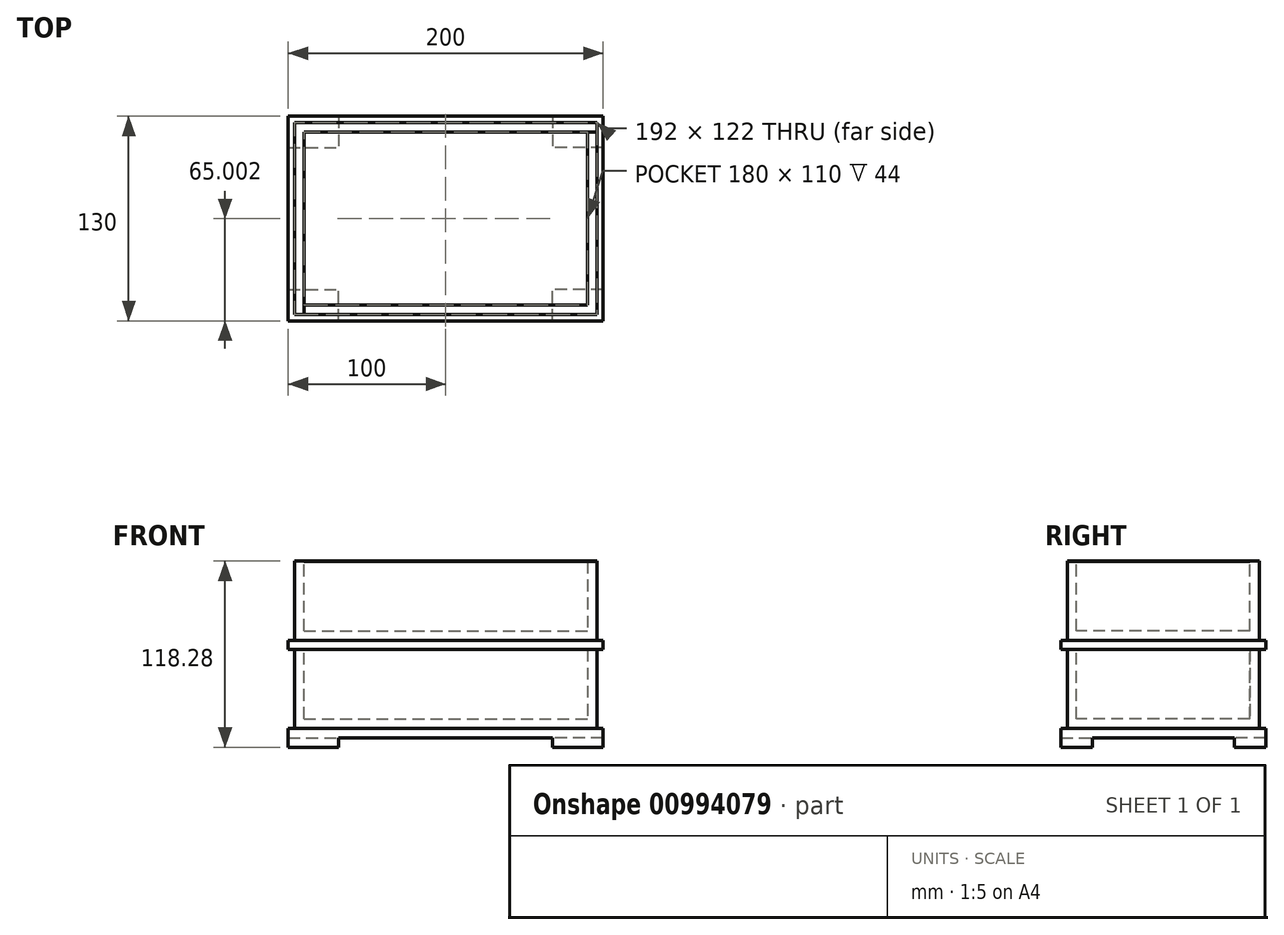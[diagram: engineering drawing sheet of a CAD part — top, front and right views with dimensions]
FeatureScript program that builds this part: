
annotation { "Feature Type Name" : "Feature", "Feature Type Description" : "" }
export const myFeature = defineFeature(function(context is Context, id is Id, definition is map)
    precondition{}
    {
        {
            var Q0;
            Q0=qCreatedBy(makeId("Top.planeOp"),FACE);
            var sketch = newSketch(context, id + "F0", { "sketchPlane" : qUnion([Q0])});
            skLineSegment(sketch, "E0.bottom", {"start": v(-113.27, 130.86) * mm, "end": v(66.73, 130.86) * mm});
            skLineSegment(sketch, "E0.top", {"start": v(-113.27, 20.86) * mm, "end": v(66.73, 20.86) * mm});
            skLineSegment(sketch, "E0.left", {"start": v(-113.27, 130.86) * mm, "end": v(-113.27, 20.86) * mm});
            skLineSegment(sketch, "E0.right", {"start": v(66.73, 130.86) * mm, "end": v(66.73, 20.86) * mm});
            skSolve(sketch);
        }
        {
            var Q0;
            Q0=makeQuery(id+"F0.imprint","IMPRINT",FACE,{"disambiguationData":[TD([[makeQuery(id+"F0.imprint","IMPRINT",EDGE,{"derivedFrom":sQuery(id+"F0.wireOp",EDGE,"E0.bottom")}),-1.0]])]});
            extrude(context, id + "F1", {"entities" : qUnion([Q0]), "depth" : 6 * mm, "offsetDistance" : 25 * mm});
        }
        {
            var Q0;
            Q0=makeQuery(id+"F1.opExtrude","SWEPT_FACE",FACE,{"disambiguationData":[OSD([sQuery(id+"F0.wireOp",EDGE,"E0.top")])]});
            var sketch = newSketch(context, id + "F2", { "sketchPlane" : qUnion([Q0])});
            skLineSegment(sketch, "E1.bottom", {"start": v(-113.27, 0) * mm, "end": v(66.73, 0) * mm});
            skLineSegment(sketch, "E1.top", {"start": v(-113.27, 50) * mm, "end": v(66.73, 50) * mm});
            skLineSegment(sketch, "E1.left", {"start": v(-113.27, 0) * mm, "end": v(-113.27, 50) * mm});
            skLineSegment(sketch, "E1.right", {"start": v(66.73, 0) * mm, "end": v(66.73, 50) * mm});
            skSolve(sketch);
        }
        {
            var Q0;
            {var subQ0=sQuery(id+"F2.wireOp",EDGE,"E1.top");Q0=makeQuery(id+"F2.imprint","IMPRINT",FACE,{"disambiguationData":[TD([[makeQuery(id+"F2.imprint","IMPRINT",EDGE,{"derivedFrom":subQ0}),-1.0]])]});}
            var Q1;
            {var subQ0=sQuery(id+"F2.wireOp",EDGE,"E1.bottom");Q1=makeQuery(id+"F2.imprint","IMPRINT",FACE,{"disambiguationData":[TD([[makeQuery(id+"F2.imprint","IMPRINT",EDGE,{"derivedFrom":subQ0}),1.0]])]});}
            extrude(context, id + "F3", {"entities" : qUnion([Q0, Q1]), "depth" : 6 * mm, "offsetDistance" : 25 * mm});
        }
        {
            var Q0;
            Q0=makeQuery(id+"F3.opExtrude","SWEPT_FACE",FACE,{"disambiguationData":[OSD([sQuery(id+"F2.wireOp",EDGE,"E1.right")])]});
            var sketch = newSketch(context, id + "F4", { "sketchPlane" : qUnion([Q0])});
            skLineSegment(sketch, "E2.bottom", {"start": v(14.86, 50) * mm, "end": v(130.86, 50) * mm});
            skLineSegment(sketch, "E2.top", {"start": v(14.86, 0) * mm, "end": v(130.86, 0) * mm});
            skLineSegment(sketch, "E2.left", {"start": v(14.86, 50) * mm, "end": v(14.86, 0) * mm});
            skLineSegment(sketch, "E2.right", {"start": v(130.86, 50) * mm, "end": v(130.86, 0) * mm});
            skSolve(sketch);
        }
        {
            var Q0;
            {var subQ2=sQuery(id+"F4.wireOp",EDGE,"E2.right");Q0=makeQuery(id+"F4.imprint","IMPRINT",FACE,{"disambiguationData":[TD([[makeQuery(id+"F4.imprint","IMPRINT",EDGE,{"derivedFrom":subQ2}),-1.0]])]});}
            var Q1;
            {var subQ2=sQuery(id+"F4.wireOp",EDGE,"E2.left");Q1=makeQuery(id+"F4.imprint","IMPRINT",FACE,{"disambiguationData":[TD([[makeQuery(id+"F4.imprint","IMPRINT",EDGE,{"derivedFrom":subQ2}),-1.0]])]});}
            extrude(context, id + "F5", {"entities" : qUnion([Q0, Q1]), "depth" : 6 * mm, "offsetDistance" : 25 * mm});
        }
        {
            var Q0;
            Q0=makeQuery(id+"F5.opExtrude","SWEPT_FACE",FACE,{"disambiguationData":[OSD([sQuery(id+"F4.wireOp",EDGE,"E2.right")])]});
            var sketch = newSketch(context, id + "F6", { "sketchPlane" : qUnion([Q0])});
            skLineSegment(sketch, "E3.bottom", {"start": v(-72.73, 0) * mm, "end": v(113.27, 0) * mm});
            skLineSegment(sketch, "E3.top", {"start": v(-72.73, 50.28) * mm, "end": v(113.27, 50.28) * mm});
            skLineSegment(sketch, "E3.left", {"start": v(-72.73, 0) * mm, "end": v(-72.73, 50.28) * mm});
            skLineSegment(sketch, "E3.right", {"start": v(113.27, 0) * mm, "end": v(113.27, 50.28) * mm});
            skSolve(sketch);
        }
        {
            var Q0;
            {var subQ3=sQuery(id+"F6.wireOp",EDGE,"E3.top");Q0=makeQuery(id+"F6.imprint","IMPRINT",FACE,{"disambiguationData":[TD([[makeQuery(id+"F6.imprint","IMPRINT",EDGE,{"derivedFrom":subQ3}),-1.0]])]});}
            var Q1;
            {var subQ1=sQuery(id+"F4.wireOp",EDGE,"E2.right");var subQ2=makeQuery(id+"F5.opExtrude","CAP_EDGE",EDGE,{"disambiguationData":[OSD([subQ1])],"isStart":true});Q1=makeQuery(id+"F6.imprint","IMPRINT",FACE,{"disambiguationData":[TD([[makeQuery(id+"F6.imprint","IMPRINT",EDGE,{"derivedFrom":subQ2}),-1.0]])]});}
            extrude(context, id + "F7", {"entities" : qUnion([Q0, Q1]), "depth" : 6 * mm, "offsetDistance" : 25 * mm});
        }
        {
            var Q0;
            Q0=makeQuery(id+"F7.opExtrude","SWEPT_FACE",FACE,{"disambiguationData":[OSD([sQuery(id+"F6.wireOp",EDGE,"E3.right")])]});
            var sketch = newSketch(context, id + "F8", { "sketchPlane" : qUnion([Q0])});
            skLineSegment(sketch, "E4.bottom", {"start": v(-136.86, 50.28) * mm, "end": v(-14.86, 50.28) * mm});
            skLineSegment(sketch, "E4.top", {"start": v(-136.86, 0) * mm, "end": v(-14.86, 0) * mm});
            skLineSegment(sketch, "E4.left", {"start": v(-136.86, 50.28) * mm, "end": v(-136.86, 0) * mm});
            skLineSegment(sketch, "E4.right", {"start": v(-14.86, 50.28) * mm, "end": v(-14.86, 0) * mm});
            skSolve(sketch);
        }
        {
            var Q0;
            {var subQ2=sQuery(id+"F8.wireOp",EDGE,"E4.right");Q0=makeQuery(id+"F8.imprint","IMPRINT",FACE,{"disambiguationData":[TD([[makeQuery(id+"F8.imprint","IMPRINT",EDGE,{"derivedFrom":subQ2}),-1.0]])]});}
            var Q1;
            {var subQ2=sQuery(id+"F8.wireOp",EDGE,"E4.left");Q1=makeQuery(id+"F8.imprint","IMPRINT",FACE,{"disambiguationData":[TD([[makeQuery(id+"F8.imprint","IMPRINT",EDGE,{"derivedFrom":subQ2}),-1.0]])]});}
            extrude(context, id + "F9", {"entities" : qUnion([Q0, Q1]), "depth" : 6 * mm, "offsetDistance" : 25 * mm});
        }
        {
            var Q0;
            Q0=makeQuery(id+"F1.opExtrude","CAP_FACE",FACE,{"disambiguationData":[OSD([sQuery(id+"F0.wireOp",EDGE,"E0.bottom"),sQuery(id+"F0.wireOp",EDGE,"E0.top"),sQuery(id+"F0.wireOp",EDGE,"E0.left"),sQuery(id+"F0.wireOp",EDGE,"E0.right")])],"isStart":true});
            var sketch = newSketch(context, id + "F10", { "sketchPlane" : qUnion([Q0])});
            skLineSegment(sketch, "E5.bottom", {"start": v(-123.27, -140.86) * mm, "end": v(76.73, -140.86) * mm});
            skLineSegment(sketch, "E5.top", {"start": v(-123.27, -10.86) * mm, "end": v(76.73, -10.86) * mm});
            skLineSegment(sketch, "E5.left", {"start": v(-123.27, -140.86) * mm, "end": v(-123.27, -10.86) * mm});
            skLineSegment(sketch, "E5.right", {"start": v(76.73, -140.86) * mm, "end": v(76.73, -10.86) * mm});
            skPoint(sketch, "E5.middle", {"position": v(-23.27, -75.86) * mm});
            skPoint(sketch, "E5.middle.positionSnap0", {"position": v(-23.27, -130.86) * mm});
            skPoint(sketch, "E5.middle.positionSnap1", {"position": v(66.73, -75.86) * mm});
            skPoint(sketch, "E5.centerSnap0", {"position": v(-23.27, -130.86) * mm});
            skPoint(sketch, "E5.centerSnap1", {"position": v(66.73, -75.86) * mm});
            skSolve(sketch);
        }
        {
            var Q0;
            Q0=makeQuery(id+"F10.imprint","IMPRINT",FACE,{"disambiguationData":[TD([[makeQuery(id+"F10.imprint","IMPRINT",EDGE,{"derivedFrom":sQuery(id+"F10.wireOp",EDGE,"E5.bottom")}),1.0]])]});
            var Q1;
            Q1=makeQuery(id+"F10.imprint","IMPRINT",FACE,{"disambiguationData":[TD([[makeQuery(id+"F10.imprint","IMPRINT",EDGE,{"derivedFrom":makeQuery(id+"F1.opExtrude","CAP_EDGE",EDGE,{"disambiguationData":[OSD([sQuery(id+"F0.wireOp",EDGE,"E0.bottom")])],"isStart":true})}),1.0]])]});
            extrude(context, id + "F11", {"entities" : qUnion([Q0, Q1]), "operationType" : NewBodyOperationType.ADD, "depth" : 6 * mm, "offsetDistance" : 25 * mm});
        }
        {
            var Q0;
            Q0=makeQuery(id+"F1.opExtrude","SWEPT_BODY",BODY,{"disambiguationData":[OSD([sQuery(id+"F0.wireOp",EDGE,"E0.bottom"),sQuery(id+"F0.wireOp",EDGE,"E0.top"),sQuery(id+"F0.wireOp",EDGE,"E0.left"),sQuery(id+"F0.wireOp",EDGE,"E0.right")])]});
            transform(context, id + "F12", {"entities" : qUnion([Q0]), "transformType" : TransformType.TRANSLATION_3D, "dx" : 0 * mm, "dy" : 0 * mm, "dz" : 56 * mm, "makeCopy" : true});
        }
        {
            var Q0;
            Q0=makeQuery(id+"F11.opExtrude","CAP_FACE",FACE,{"disambiguationData":[OSD([sQuery(id+"F10.wireOp",EDGE,"E5.bottom"),sQuery(id+"F10.wireOp",EDGE,"E5.top"),sQuery(id+"F10.wireOp",EDGE,"E5.left"),sQuery(id+"F10.wireOp",EDGE,"E5.right")])],"isStart":false});
            var sketch = newSketch(context, id + "F13", { "sketchPlane" : qUnion([Q0])});
            skLineSegment(sketch, "E6.bottom", {"start": v(76.73, -140.86) * mm, "end": v(44.73, -140.86) * mm});
            skLineSegment(sketch, "E6.top", {"start": v(76.73, -120.86) * mm, "end": v(44.73, -120.86) * mm});
            skLineSegment(sketch, "E6.left", {"start": v(76.73, -140.86) * mm, "end": v(76.73, -120.86) * mm});
            skLineSegment(sketch, "E6.right", {"start": v(44.73, -140.86) * mm, "end": v(44.73, -120.86) * mm});
            skLineSegment(sketch, "E7.bottom", {"start": v(-123.27, -140.86) * mm, "end": v(-91.27, -140.86) * mm});
            skLineSegment(sketch, "E7.top", {"start": v(-123.27, -120.86) * mm, "end": v(-91.27, -120.86) * mm});
            skLineSegment(sketch, "E7.left", {"start": v(-123.27, -140.86) * mm, "end": v(-123.27, -120.86) * mm});
            skLineSegment(sketch, "E7.right", {"start": v(-91.27, -140.86) * mm, "end": v(-91.27, -120.86) * mm});
            skLineSegment(sketch, "E8.bottom", {"start": v(-123.27, -10.86) * mm, "end": v(-91.27, -10.86) * mm});
            skLineSegment(sketch, "E8.top", {"start": v(-123.27, -30.86) * mm, "end": v(-91.27, -30.86) * mm});
            skLineSegment(sketch, "E8.left", {"start": v(-123.27, -10.86) * mm, "end": v(-123.27, -30.86) * mm});
            skLineSegment(sketch, "E8.right", {"start": v(-91.27, -10.86) * mm, "end": v(-91.27, -30.86) * mm});
            skLineSegment(sketch, "E9.bottom", {"start": v(76.73, -10.86) * mm, "end": v(44.73, -10.86) * mm});
            skLineSegment(sketch, "E9.top", {"start": v(76.73, -30.86) * mm, "end": v(44.73, -30.86) * mm});
            skLineSegment(sketch, "E9.left", {"start": v(76.73, -10.86) * mm, "end": v(76.73, -30.86) * mm});
            skLineSegment(sketch, "E9.right", {"start": v(44.73, -10.86) * mm, "end": v(44.73, -30.86) * mm});
            skSolve(sketch);
        }
        {
            var Q0;
            Q0=makeQuery(id+"F13.imprint","IMPRINT",FACE,{"disambiguationData":[TD([[makeQuery(id+"F13.imprint","IMPRINT",EDGE,{"derivedFrom":sQuery(id+"F13.wireOp",EDGE,"E6.bottom")}),1.0]])]});
            var Q1;
            Q1=makeQuery(id+"F13.imprint","IMPRINT",FACE,{"disambiguationData":[TD([[makeQuery(id+"F13.imprint","IMPRINT",EDGE,{"derivedFrom":sQuery(id+"F13.wireOp",EDGE,"E7.bottom")}),1.0]])]});
            var Q2;
            Q2=makeQuery(id+"F13.imprint","IMPRINT",FACE,{"disambiguationData":[TD([[makeQuery(id+"F13.imprint","IMPRINT",EDGE,{"derivedFrom":sQuery(id+"F13.wireOp",EDGE,"E8.bottom")}),-1.0]])]});
            var Q3;
            Q3=makeQuery(id+"F13.imprint","IMPRINT",FACE,{"disambiguationData":[TD([[makeQuery(id+"F13.imprint","IMPRINT",EDGE,{"derivedFrom":sQuery(id+"F13.wireOp",EDGE,"E9.bottom")}),-1.0]])]});
            extrude(context, id + "F14", {"entities" : qUnion([Q0, Q1, Q2, Q3]), "operationType" : NewBodyOperationType.ADD, "depth" : 6 * mm, "offsetDistance" : 25 * mm});
        }
    });
